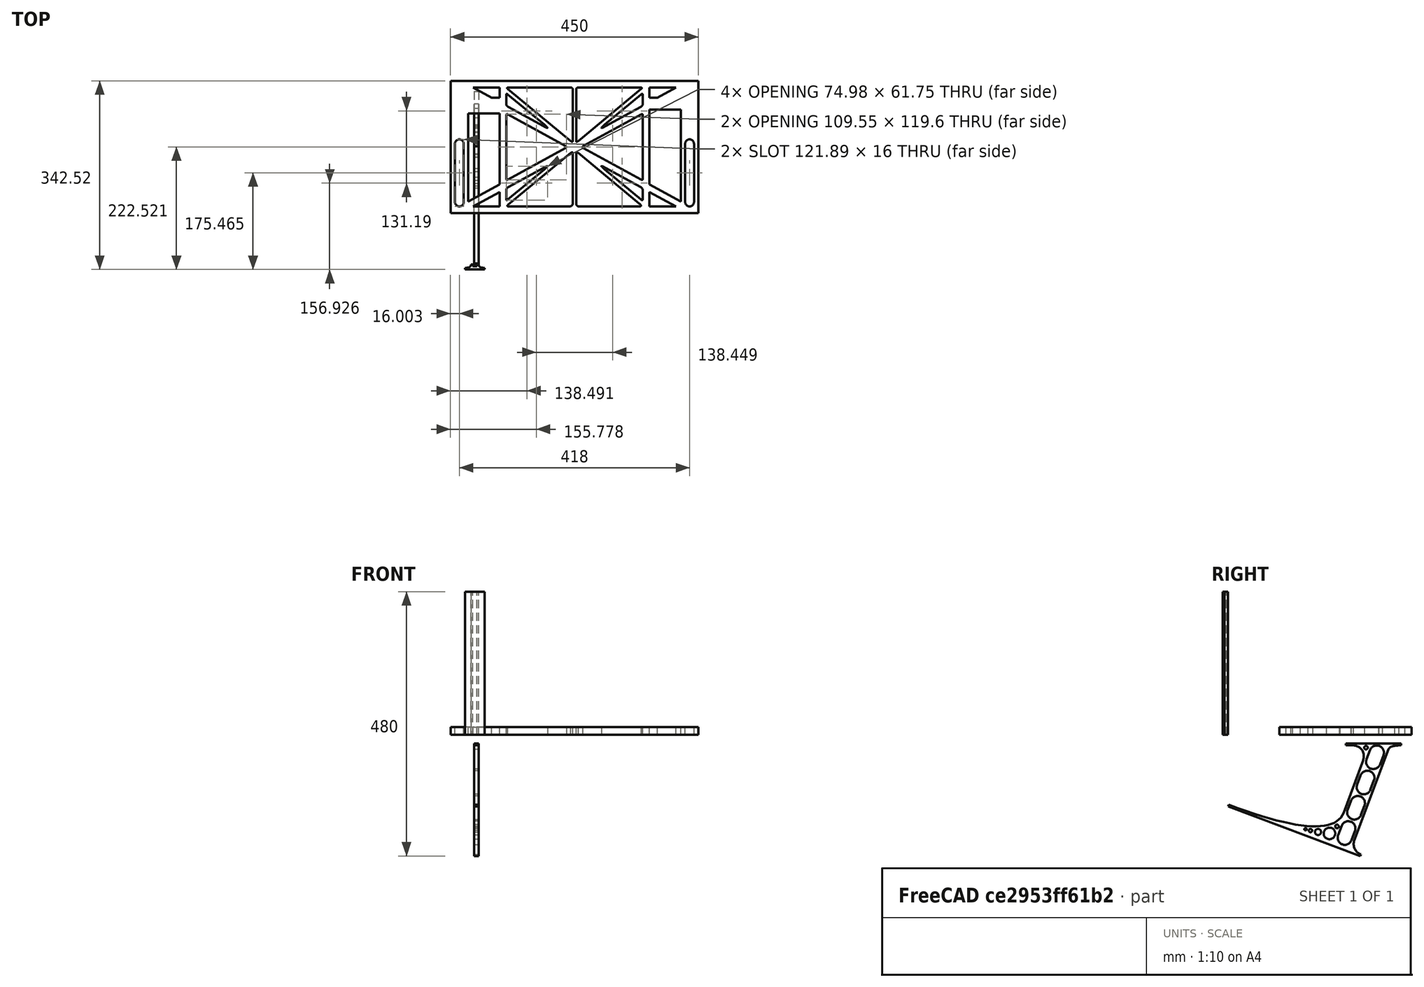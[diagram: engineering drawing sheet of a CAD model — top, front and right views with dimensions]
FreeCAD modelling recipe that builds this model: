
FCSTD DOCUMENT  (FreeCAD 0.19R0.19.2)
Label: laptopStand093
License: All rights reserved
LicenseURL: http://en.wikipedia.org/wiki/All_rights_reserved
objects: Sketcher::SketchObject×3, Part::Extrusion×3
note: 6 computed .brp shape members not serialized (recipe doc carries the construction recipe); baked Part::Feature solids carry a one-line shape summary decoded from their .brp

FEATURE [Sketcher::SketchObject] Sketch
  FullyConstrained = false
  sketch-geometry (252):
    g0: LineSegment StartX=-10.9272 StartY=-82.7794 StartZ=0 EndX=46.0728 EndY=-51.4823 EndZ=0
    g1: LineSegment StartX=366.073 StartY=-91.7794 StartZ=0 EndX=318.073 EndY=-65.424 EndZ=0
    g2: LineSegment StartX=-10.9272 StartY=77.3346 StartZ=0 EndX=-10.9272 EndY=-82.7794 EndZ=0
    g3: LineSegment StartX=375.073 StartY=-82.7794 StartZ=0 EndX=375.073 EndY=83.9235 EndZ=0
    g4: LineSegment StartX=-1.92719 StartY=-91.7794 StartZ=0 EndX=46.0728 EndY=-91.7794 EndZ=0
    g5: LineSegment StartX=318.073 StartY=124.221 StartZ=0 EndX=366.073 EndY=124.221 EndZ=0
    g6: LineSegment StartX=318.073 StartY=83.9235 StartZ=0 EndX=318.073 EndY=-51.4823 EndZ=0
    g7: LineSegment StartX=318.073 StartY=-51.4823 StartZ=0 EndX=375.073 EndY=-82.7794 EndZ=0
    g8: LineSegment StartX=318.073 StartY=-65.424 StartZ=0 EndX=318.073 EndY=-91.7794 EndZ=0
    g9: LineSegment StartX=318.073 StartY=-91.7794 StartZ=0 EndX=366.073 EndY=-91.7794 EndZ=0
    g10: LineSegment StartX=46.0728 StartY=-65.424 StartZ=0 EndX=-1.92719 EndY=-91.7794 EndZ=0
    g11: LineSegment StartX=46.0728 StartY=-65.424 StartZ=0 EndX=46.0728 EndY=-91.7794 EndZ=0
    g12: LineSegment StartX=46.0728 StartY=77.3346 StartZ=0 EndX=46.0728 EndY=-51.4823 EndZ=0
    g13: LineSegment StartX=-42.9272 StartY=136.221 StartZ=0 EndX=-42.9272 EndY=-103.779 EndZ=0
    g14: LineSegment StartX=407.073 StartY=136.221 StartZ=0 EndX=407.073 EndY=-103.779 EndZ=0
    g15: ArcOfCircle CenterX=-26.9272 CenterY=22.1087 CenterZ=0 NormalX=0 NormalY=0 NormalZ=1 AngleXU=0 Radius=8 StartAngle=1e-16 EndAngle=3.14159
    g16: ArcOfCircle CenterX=-26.9272 CenterY=-83.7794 CenterZ=0 NormalX=0 NormalY=0 NormalZ=1 AngleXU=0 Radius=8 StartAngle=3.14159 EndAngle=6.28319
    g17: LineSegment StartX=-34.9272 StartY=22.1087 StartZ=0 EndX=-34.9272 EndY=-83.7794 EndZ=0
    g18: LineSegment StartX=-18.9272 StartY=22.1087 StartZ=0 EndX=-18.9272 EndY=-83.7794 EndZ=0
    g19: ArcOfCircle CenterX=391.073 CenterY=22.1087 CenterZ=0 NormalX=0 NormalY=0 NormalZ=1 AngleXU=0 Radius=8 StartAngle=-4.4e-15 EndAngle=3.14159
    g20: LineSegment StartX=399.073 StartY=22.1087 StartZ=0 EndX=399.073 EndY=-83.7794 EndZ=0
    g21: LineSegment StartX=383.073 StartY=22.1087 StartZ=0 EndX=383.073 EndY=-83.7794 EndZ=0
    g22: ArcOfCircle CenterX=391.073 CenterY=-83.7794 CenterZ=0 NormalX=0 NormalY=0 NormalZ=1 AngleXU=0 Radius=8 StartAngle=3.14159 EndAngle=6.28319
    g23: Circle CenterX=175.022 CenterY=27.0628 CenterZ=0 NormalX=0 NormalY=0 NormalZ=1 AngleXU=0 Radius=1
    g24: Circle CenterX=179.022 CenterY=24.8665 CenterZ=0 NormalX=0 NormalY=0 NormalZ=1 AngleXU=0 Radius=1
    g25: Circle CenterX=179.022 CenterY=27.0628 CenterZ=0 NormalX=0 NormalY=0 NormalZ=1 AngleXU=0 Radius=1
    g26: BSplineCurve PolesCount=3 KnotsCount=2 Degree=2 IsPeriodic=0
    g27: GeomPoint X=175.022 Y=27.0628 Z=0
    g28: GeomPoint X=179.022 Y=27.0628 Z=0
    g29: Circle CenterX=189.124 CenterY=27.0628 CenterZ=0 NormalX=0 NormalY=0 NormalZ=1 AngleXU=0 Radius=1
    g30: Circle CenterX=185.124 CenterY=24.8665 CenterZ=0 NormalX=0 NormalY=0 NormalZ=1 AngleXU=0 Radius=1
    g31: Circle CenterX=185.124 CenterY=27.0628 CenterZ=0 NormalX=0 NormalY=0 NormalZ=1 AngleXU=0 Radius=1
    g32: BSplineCurve PolesCount=3 KnotsCount=2 Degree=2 IsPeriodic=0
    g33: GeomPoint X=189.124 Y=27.0628 Z=0
    g34: GeomPoint X=185.124 Y=27.0628 Z=0
    g35: Circle CenterX=175.022 CenterY=5.37834 CenterZ=0 NormalX=0 NormalY=0 NormalZ=1 AngleXU=0 Radius=1
    g36: Circle CenterX=179.022 CenterY=7.57463 CenterZ=0 NormalX=0 NormalY=0 NormalZ=1 AngleXU=0 Radius=1
    g37: Circle CenterX=179.022 CenterY=5.34704 CenterZ=0 NormalX=0 NormalY=0 NormalZ=1 AngleXU=0 Radius=1
    g38: BSplineCurve PolesCount=3 KnotsCount=2 Degree=2 IsPeriodic=0
    g39: GeomPoint X=175.022 Y=5.37834 Z=0
    g40: GeomPoint X=179.022 Y=5.34704 Z=0
    g41: Circle CenterX=189.124 CenterY=5.37834 CenterZ=0 NormalX=0 NormalY=0 NormalZ=1 AngleXU=0 Radius=1
    g42: Circle CenterX=185.124 CenterY=7.57463 CenterZ=0 NormalX=0 NormalY=0 NormalZ=1 AngleXU=0 Radius=1
    g43: Circle CenterX=185.124 CenterY=5.34704 CenterZ=0 NormalX=0 NormalY=0 NormalZ=1 AngleXU=0 Radius=1
    g44: BSplineCurve PolesCount=3 KnotsCount=2 Degree=2 IsPeriodic=0
    g45: GeomPoint X=189.124 Y=5.37834 Z=0
    g46: GeomPoint X=185.124 Y=5.34704 Z=0
    g47: Circle CenterX=165.871 CenterY=18.1458 CenterZ=0 NormalX=0 NormalY=0 NormalZ=1 AngleXU=0 Radius=1
    g48: Circle CenterX=169.377 CenterY=16.2206 CenterZ=0 NormalX=0 NormalY=0 NormalZ=1 AngleXU=0 Radius=1
    g49: Circle CenterX=165.871 CenterY=14.2954 CenterZ=0 NormalX=0 NormalY=0 NormalZ=1 AngleXU=0 Radius=1
    g50: BSplineCurve PolesCount=3 KnotsCount=2 Degree=2 IsPeriodic=0
    g51: GeomPoint X=165.871 Y=18.1458 Z=0
    g52: GeomPoint X=165.871 Y=14.2954 Z=0
    g53: Circle CenterX=198.275 CenterY=18.1458 CenterZ=0 NormalX=0 NormalY=0 NormalZ=1 AngleXU=0 Radius=1
    g54: Circle CenterX=194.768 CenterY=16.2206 CenterZ=0 NormalX=0 NormalY=0 NormalZ=1 AngleXU=0 Radius=1
    g55: Circle CenterX=198.275 CenterY=14.2954 CenterZ=0 NormalX=0 NormalY=0 NormalZ=1 AngleXU=0 Radius=1
    g56: BSplineCurve PolesCount=3 KnotsCount=2 Degree=2 IsPeriodic=0
    g57: GeomPoint X=198.275 Y=18.1458 Z=0
    g58: GeomPoint X=198.275 Y=14.2954 Z=0
    g59: LineSegment StartX=407.073 StartY=-103.779 StartZ=0 EndX=-42.9272 EndY=-103.779 EndZ=0
    g60: LineSegment StartX=407.073 StartY=136.221 StartZ=0 EndX=-42.9272 EndY=136.221 EndZ=0
    g61: LineSegment StartX=46.0728 StartY=77.3346 StartZ=0 EndX=-10.9272 EndY=77.3346 EndZ=0
    g62: LineSegment StartX=46.0728 StartY=105.865 StartZ=0 EndX=31.5028 EndY=105.865 EndZ=0
    g63: LineSegment StartX=46.0728 StartY=124.221 StartZ=0 EndX=46.0728 EndY=105.865 EndZ=0
    g64: LineSegment StartX=-1.92719 StartY=124.221 StartZ=0 EndX=31.5028 EndY=105.865 EndZ=0
    g65: LineSegment StartX=46.0728 StartY=124.221 StartZ=0 EndX=-1.92719 EndY=124.221 EndZ=0
    g66: LineSegment StartX=318.073 StartY=83.9235 StartZ=0 EndX=375.073 EndY=83.9235 EndZ=0
    g67: LineSegment StartX=318.073 StartY=105.865 StartZ=0 EndX=332.643 EndY=105.865 EndZ=0
    g68: LineSegment StartX=332.643 StartY=105.865 StartZ=0 EndX=366.073 EndY=124.221 EndZ=0
    g69: LineSegment StartX=318.073 StartY=124.221 StartZ=0 EndX=318.073 EndY=105.865 EndZ=0
    g70: Circle CenterX=125.607 CenterY=54.1951 CenterZ=0 NormalX=0 NormalY=0 NormalZ=1 AngleXU=0 Radius=1
    g71: Circle CenterX=139.632 CenterY=46.4944 CenterZ=0 NormalX=0 NormalY=0 NormalZ=1 AngleXU=0 Radius=1
    g72: Circle CenterX=127.326 CenterY=56.7187 CenterZ=0 NormalX=0 NormalY=0 NormalZ=1 AngleXU=0 Radius=1
    g73: BSplineCurve PolesCount=3 KnotsCount=2 Degree=2 IsPeriodic=0
    g74: GeomPoint X=125.607 Y=54.1951 Z=0
    g75: GeomPoint X=127.326 Y=56.7187 Z=0
    g76: Circle CenterX=236.821 CenterY=56.7187 CenterZ=0 NormalX=0 NormalY=0 NormalZ=1 AngleXU=0 Radius=1
    g77: Circle CenterX=224.513 CenterY=46.4944 CenterZ=0 NormalX=0 NormalY=0 NormalZ=1 AngleXU=0 Radius=1
    g78: Circle CenterX=238.538 CenterY=54.1951 CenterZ=0 NormalX=0 NormalY=0 NormalZ=1 AngleXU=0 Radius=1
    g79: BSplineCurve PolesCount=3 KnotsCount=2 Degree=2 IsPeriodic=0
    g80: GeomPoint X=236.821 Y=56.7187 Z=0
    g81: GeomPoint X=238.538 Y=54.1951 Z=0
    g82: Circle CenterX=238.538 CenterY=-21.7539 CenterZ=0 NormalX=0 NormalY=0 NormalZ=1 AngleXU=0 Radius=1
    g83: Circle CenterX=224.513 CenterY=-14.0532 CenterZ=0 NormalX=0 NormalY=0 NormalZ=1 AngleXU=0 Radius=1
    g84: Circle CenterX=236.821 CenterY=-24.2775 CenterZ=0 NormalX=0 NormalY=0 NormalZ=1 AngleXU=0 Radius=1
    g85: BSplineCurve PolesCount=3 KnotsCount=2 Degree=2 IsPeriodic=0
    g86: GeomPoint X=238.538 Y=-21.7539 Z=0
    g87: GeomPoint X=236.821 Y=-24.2775 Z=0
    g88: Circle CenterX=125.607 CenterY=-21.7539 CenterZ=0 NormalX=0 NormalY=0 NormalZ=1 AngleXU=0 Radius=1
    g89: Circle CenterX=139.632 CenterY=-14.0532 CenterZ=0 NormalX=0 NormalY=0 NormalZ=1 AngleXU=0 Radius=1
    g90: Circle CenterX=127.325 CenterY=-24.2775 CenterZ=0 NormalX=0 NormalY=0 NormalZ=1 AngleXU=0 Radius=1
    g91: BSplineCurve PolesCount=3 KnotsCount=2 Degree=2 IsPeriodic=0
    g92: GeomPoint X=125.607 Y=-21.7539 Z=0
    g93: GeomPoint X=127.325 Y=-24.2775 Z=0
    g94: Circle CenterX=302.996 CenterY=111.695 CenterZ=0 NormalX=0 NormalY=0 NormalZ=1 AngleXU=0 Radius=1
    g95: Circle CenterX=306.073 CenterY=114.251 CenterZ=0 NormalX=0 NormalY=0 NormalZ=1 AngleXU=0 Radius=1
    g96: Circle CenterX=306.073 CenterY=110.251 CenterZ=0 NormalX=0 NormalY=0 NormalZ=1 AngleXU=0 Radius=1
    g97: BSplineCurve PolesCount=3 KnotsCount=2 Degree=2 IsPeriodic=0
    g98: GeomPoint X=302.996 Y=111.695 Z=0
    g99: GeomPoint X=306.073 Y=110.251 Z=0
    g100: Circle CenterX=306.073 CenterY=95.2763 CenterZ=0 NormalX=0 NormalY=0 NormalZ=1 AngleXU=0 Radius=1
    g101: Circle CenterX=306.073 CenterY=91.2763 CenterZ=0 NormalX=0 NormalY=0 NormalZ=1 AngleXU=0 Radius=1
    g102: Circle CenterX=302.567 CenterY=89.3511 CenterZ=0 NormalX=0 NormalY=0 NormalZ=1 AngleXU=0 Radius=1
    g103: BSplineCurve PolesCount=3 KnotsCount=2 Degree=2 IsPeriodic=0
    g104: GeomPoint X=306.073 Y=95.2763 Z=0
    g105: GeomPoint X=302.567 Y=89.3511 Z=0
    g106: LineSegment StartX=306.073 StartY=110.251 StartZ=0 EndX=306.073 EndY=95.2763 EndZ=0
    g107: LineSegment StartX=302.996 StartY=111.695 StartZ=0 EndX=236.821 EndY=56.7187 EndZ=0
    g108: LineSegment StartX=238.538 StartY=54.1951 StartZ=0 EndX=302.567 EndY=89.3511 EndZ=0
    g109: Circle CenterX=61.1496 CenterY=111.695 CenterZ=0 NormalX=0 NormalY=0 NormalZ=1 AngleXU=0 Radius=1
    g110: Circle CenterX=58.0728 CenterY=114.251 CenterZ=0 NormalX=0 NormalY=0 NormalZ=1 AngleXU=0 Radius=1
    g111: Circle CenterX=58.0728 CenterY=110.251 CenterZ=0 NormalX=0 NormalY=0 NormalZ=1 AngleXU=0 Radius=1
    g112: BSplineCurve PolesCount=3 KnotsCount=2 Degree=2 IsPeriodic=0
    g113: GeomPoint X=61.1496 Y=111.695 Z=0
    g114: GeomPoint X=58.0728 Y=110.251 Z=0
    g115: Circle CenterX=61.5791 CenterY=89.3511 CenterZ=0 NormalX=0 NormalY=0 NormalZ=1 AngleXU=0 Radius=1
    g116: Circle CenterX=58.0728 CenterY=91.2763 CenterZ=0 NormalX=0 NormalY=0 NormalZ=1 AngleXU=0 Radius=1
    g117: Circle CenterX=58.0728 CenterY=95.2763 CenterZ=0 NormalX=0 NormalY=0 NormalZ=1 AngleXU=0 Radius=1
    g118: BSplineCurve PolesCount=3 KnotsCount=2 Degree=2 IsPeriodic=0
    g119: GeomPoint X=61.5791 Y=89.3511 Z=0
    g120: GeomPoint X=58.0728 Y=95.2763 Z=0
    g121: LineSegment StartX=58.0728 StartY=110.251 StartZ=0 EndX=58.0728 EndY=95.2763 EndZ=0
    g122: LineSegment StartX=61.1496 StartY=111.695 StartZ=0 EndX=127.326 EndY=56.7187 EndZ=0
    g123: LineSegment StartX=125.607 StartY=54.1951 StartZ=0 EndX=61.5791 EndY=89.3511 EndZ=0
    g124: Circle CenterX=61.5791 CenterY=-56.9099 CenterZ=0 NormalX=0 NormalY=0 NormalZ=1 AngleXU=0 Radius=1
    g125: Circle CenterX=58.0728 CenterY=-58.8351 CenterZ=0 NormalX=0 NormalY=0 NormalZ=1 AngleXU=0 Radius=1
    g126: Circle CenterX=58.0728 CenterY=-62.8351 CenterZ=0 NormalX=0 NormalY=0 NormalZ=1 AngleXU=0 Radius=1
    g127: BSplineCurve PolesCount=3 KnotsCount=2 Degree=2 IsPeriodic=0
    g128: GeomPoint X=61.5791 Y=-56.9099 Z=0
    g129: GeomPoint X=58.0728 Y=-62.8351 Z=0
    g130: Circle CenterX=58.0728 CenterY=-77.8102 CenterZ=0 NormalX=0 NormalY=0 NormalZ=1 AngleXU=0 Radius=1
    g131: Circle CenterX=58.0728 CenterY=-81.8102 CenterZ=0 NormalX=0 NormalY=0 NormalZ=1 AngleXU=0 Radius=1
    g132: Circle CenterX=61.1496 CenterY=-79.2541 CenterZ=0 NormalX=0 NormalY=0 NormalZ=1 AngleXU=0 Radius=1
    g133: BSplineCurve PolesCount=3 KnotsCount=2 Degree=2 IsPeriodic=0
    g134: GeomPoint X=58.0728 Y=-77.8102 Z=0
    g135: GeomPoint X=61.1496 Y=-79.2541 Z=0
    g136: LineSegment StartX=58.0728 StartY=-62.8351 StartZ=0 EndX=58.0728 EndY=-77.8102 EndZ=0
    g137: LineSegment StartX=61.1496 StartY=-79.2541 StartZ=0 EndX=127.325 EndY=-24.2775 EndZ=0
    g138: LineSegment StartX=125.607 StartY=-21.7539 StartZ=0 EndX=61.5791 EndY=-56.9099 EndZ=0
    g139: Circle CenterX=302.567 CenterY=-56.9099 CenterZ=0 NormalX=0 NormalY=0 NormalZ=1 AngleXU=0 Radius=1
    g140: Circle CenterX=306.073 CenterY=-58.8351 CenterZ=0 NormalX=0 NormalY=0 NormalZ=1 AngleXU=0 Radius=1
    g141: Circle CenterX=306.073 CenterY=-62.8351 CenterZ=0 NormalX=0 NormalY=0 NormalZ=1 AngleXU=0 Radius=1
    g142: BSplineCurve PolesCount=3 KnotsCount=2 Degree=2 IsPeriodic=0
    g143: GeomPoint X=302.567 Y=-56.9099 Z=0
    g144: GeomPoint X=306.073 Y=-62.8351 Z=0
    g145: Circle CenterX=302.996 CenterY=-79.2541 CenterZ=0 NormalX=0 NormalY=0 NormalZ=1 AngleXU=0 Radius=1
    g146: Circle CenterX=306.073 CenterY=-81.8102 CenterZ=0 NormalX=0 NormalY=0 NormalZ=1 AngleXU=0 Radius=1
    g147: Circle CenterX=306.073 CenterY=-77.8102 CenterZ=0 NormalX=0 NormalY=0 NormalZ=1 AngleXU=0 Radius=1
    g148: BSplineCurve PolesCount=3 KnotsCount=2 Degree=2 IsPeriodic=0
    g149: GeomPoint X=302.996 Y=-79.2541 Z=0
    g150: GeomPoint X=306.073 Y=-77.8102 Z=0
    g151: LineSegment StartX=306.073 StartY=-62.8351 StartZ=0 EndX=306.073 EndY=-77.8102 EndZ=0
    g152: LineSegment StartX=302.996 StartY=-79.2541 StartZ=0 EndX=236.821 EndY=-24.2775 EndZ=0
    g153: LineSegment StartX=238.538 StartY=-21.7539 StartZ=0 EndX=302.567 EndY=-56.9099 EndZ=0
    g154: Circle CenterX=61.6457 CenterY=-88.8112 CenterZ=0 NormalX=0 NormalY=0 NormalZ=1 AngleXU=0 Radius=1
    g155: Circle CenterX=58.0728 CenterY=-91.7794 CenterZ=0 NormalX=0 NormalY=0 NormalZ=1 AngleXU=0 Radius=1
    g156: Circle CenterX=63.9135 CenterY=-91.7794 CenterZ=0 NormalX=0 NormalY=0 NormalZ=1 AngleXU=0 Radius=1
    g157: BSplineCurve PolesCount=3 KnotsCount=2 Degree=2 IsPeriodic=0
    g158: GeomPoint X=61.6457 Y=-88.8112 Z=0
    g159: GeomPoint X=63.9135 Y=-91.7794 Z=0
    g160: Circle CenterX=179.022 CenterY=-85.8163 CenterZ=0 NormalX=0 NormalY=0 NormalZ=1 AngleXU=0 Radius=1
    g161: Circle CenterX=179.022 CenterY=-91.7794 CenterZ=0 NormalX=0 NormalY=0 NormalZ=1 AngleXU=0 Radius=1
    g162: Circle CenterX=171.895 CenterY=-91.7794 CenterZ=0 NormalX=0 NormalY=0 NormalZ=1 AngleXU=0 Radius=1
    g163: BSplineCurve PolesCount=3 KnotsCount=2 Degree=2 IsPeriodic=0
    g164: GeomPoint X=179.022 Y=-85.8163 Z=0
    g165: GeomPoint X=171.895 Y=-91.7794 Z=0
    g166: Circle CenterX=185.124 CenterY=-86.2028 CenterZ=0 NormalX=0 NormalY=0 NormalZ=1 AngleXU=0 Radius=1
    g167: Circle CenterX=185.124 CenterY=-91.7794 CenterZ=0 NormalX=0 NormalY=0 NormalZ=1 AngleXU=0 Radius=1
    g168: Circle CenterX=191.747 CenterY=-91.7794 CenterZ=0 NormalX=0 NormalY=0 NormalZ=1 AngleXU=0 Radius=1
    g169: BSplineCurve PolesCount=3 KnotsCount=2 Degree=2 IsPeriodic=0
    g170: GeomPoint X=185.124 Y=-86.2028 Z=0
    g171: GeomPoint X=191.747 Y=-91.7794 Z=0
    g172: Circle CenterX=299.888 CenterY=-86.6413 CenterZ=0 NormalX=0 NormalY=0 NormalZ=1 AngleXU=0 Radius=1
    g173: Circle CenterX=306.073 CenterY=-91.7794 CenterZ=0 NormalX=0 NormalY=0 NormalZ=1 AngleXU=0 Radius=1
    g174: Circle CenterX=298.776 CenterY=-91.7794 CenterZ=0 NormalX=0 NormalY=0 NormalZ=1 AngleXU=0 Radius=1
    g175: BSplineCurve PolesCount=3 KnotsCount=2 Degree=2 IsPeriodic=0
    g176: GeomPoint X=299.888 Y=-86.6413 Z=0
    g177: GeomPoint X=298.776 Y=-91.7794 Z=0
    g178: LineSegment StartX=189.124 StartY=5.37834 StartZ=0 EndX=299.888 EndY=-86.6413 EndZ=0
    g179: LineSegment StartX=298.776 StartY=-91.7794 StartZ=0 EndX=191.747 EndY=-91.7794 EndZ=0
    g180: LineSegment StartX=185.124 StartY=-86.2028 StartZ=0 EndX=185.124 EndY=5.34704 EndZ=0
    g181: LineSegment StartX=179.022 StartY=5.34704 StartZ=0 EndX=179.022 EndY=-85.8163 EndZ=0
    g182: LineSegment StartX=171.895 StartY=-91.7794 StartZ=0 EndX=63.9135 EndY=-91.7794 EndZ=0
    g183: LineSegment StartX=61.6457 StartY=-88.8112 StartZ=0 EndX=175.022 EndY=5.37834 EndZ=0
    g184: Circle CenterX=302.073 CenterY=124.221 CenterZ=0 NormalX=0 NormalY=0 NormalZ=1 AngleXU=0 Radius=1
    g185: Circle CenterX=306.073 CenterY=124.221 CenterZ=0 NormalX=0 NormalY=0 NormalZ=1 AngleXU=0 Radius=1
    g186: Circle CenterX=302.996 CenterY=121.665 CenterZ=0 NormalX=0 NormalY=0 NormalZ=1 AngleXU=0 Radius=1
    g187: BSplineCurve PolesCount=3 KnotsCount=2 Degree=2 IsPeriodic=0
    g188: GeomPoint X=302.073 Y=124.221 Z=0
    g189: GeomPoint X=302.996 Y=121.665 Z=0
    g190: Circle CenterX=189.124 CenterY=124.221 CenterZ=0 NormalX=0 NormalY=0 NormalZ=1 AngleXU=0 Radius=1
    g191: Circle CenterX=185.124 CenterY=124.221 CenterZ=0 NormalX=0 NormalY=0 NormalZ=1 AngleXU=0 Radius=1
    g192: Circle CenterX=185.124 CenterY=120.221 CenterZ=0 NormalX=0 NormalY=0 NormalZ=1 AngleXU=0 Radius=1
    g193: BSplineCurve PolesCount=3 KnotsCount=2 Degree=2 IsPeriodic=0
    g194: GeomPoint X=189.124 Y=124.221 Z=0
    g195: GeomPoint X=185.124 Y=120.221 Z=0
    g196: Circle CenterX=175.022 CenterY=124.221 CenterZ=0 NormalX=0 NormalY=0 NormalZ=1 AngleXU=0 Radius=1
    g197: Circle CenterX=179.022 CenterY=124.221 CenterZ=0 NormalX=0 NormalY=0 NormalZ=1 AngleXU=0 Radius=1
    g198: Circle CenterX=179.022 CenterY=120.221 CenterZ=0 NormalX=0 NormalY=0 NormalZ=1 AngleXU=0 Radius=1
    g199: BSplineCurve PolesCount=3 KnotsCount=2 Degree=2 IsPeriodic=0
    g200: GeomPoint X=175.022 Y=124.221 Z=0
    g201: GeomPoint X=179.022 Y=120.221 Z=0
    g202: Circle CenterX=62.0728 CenterY=124.221 CenterZ=0 NormalX=0 NormalY=0 NormalZ=1 AngleXU=0 Radius=1
    g203: Circle CenterX=58.0728 CenterY=124.221 CenterZ=0 NormalX=0 NormalY=0 NormalZ=1 AngleXU=0 Radius=1
    g204: Circle CenterX=61.1496 CenterY=121.665 CenterZ=0 NormalX=0 NormalY=0 NormalZ=1 AngleXU=0 Radius=1
    g205: BSplineCurve PolesCount=3 KnotsCount=2 Degree=2 IsPeriodic=0
    g206: GeomPoint X=62.0728 Y=124.221 Z=0
    g207: GeomPoint X=61.1496 Y=121.665 Z=0
    g208: LineSegment StartX=62.0728 StartY=124.221 StartZ=0 EndX=175.022 EndY=124.221 EndZ=0
    g209: LineSegment StartX=179.022 StartY=120.221 StartZ=0 EndX=179.022 EndY=27.0628 EndZ=0
    g210: LineSegment StartX=185.124 StartY=27.0628 StartZ=0 EndX=185.124 EndY=120.221 EndZ=0
    g211: LineSegment StartX=189.124 StartY=124.221 StartZ=0 EndX=302.073 EndY=124.221 EndZ=0
    g212: LineSegment StartX=302.996 StartY=121.665 StartZ=0 EndX=189.124 EndY=27.0628 EndZ=0
    g213: LineSegment StartX=175.022 StartY=27.0628 StartZ=0 EndX=61.1496 EndY=121.665 EndZ=0
    g214: Circle CenterX=61.5791 CenterY=75.4095 CenterZ=0 NormalX=0 NormalY=0 NormalZ=1 AngleXU=0 Radius=1
    g215: Circle CenterX=58.0728 CenterY=77.3346 CenterZ=0 NormalX=0 NormalY=0 NormalZ=1 AngleXU=0 Radius=1
    g216: Circle CenterX=58.0728 CenterY=73.3346 CenterZ=0 NormalX=0 NormalY=0 NormalZ=1 AngleXU=0 Radius=1
    g217: BSplineCurve PolesCount=3 KnotsCount=2 Degree=2 IsPeriodic=0
    g218: GeomPoint X=61.5791 Y=75.4095 Z=0
    g219: GeomPoint X=58.0728 Y=73.3346 Z=0
    g220: Circle CenterX=58.0728 CenterY=-40.8935 CenterZ=0 NormalX=0 NormalY=0 NormalZ=1 AngleXU=0 Radius=1
    g221: Circle CenterX=58.0728 CenterY=-44.8935 CenterZ=0 NormalX=0 NormalY=0 NormalZ=1 AngleXU=0 Radius=1
    g222: Circle CenterX=61.5791 CenterY=-42.9683 CenterZ=0 NormalX=0 NormalY=0 NormalZ=1 AngleXU=0 Radius=1
    g223: BSplineCurve PolesCount=3 KnotsCount=2 Degree=2 IsPeriodic=0
    g224: GeomPoint X=58.0728 Y=-40.8935 Z=0
    g225: GeomPoint X=61.5791 Y=-42.9683 Z=0
    g226: LineSegment StartX=61.5791 StartY=-42.9683 StartZ=0 EndX=165.871 EndY=14.2954 EndZ=0
    g227: LineSegment StartX=165.871 StartY=18.1458 StartZ=0 EndX=61.5791 EndY=75.4095 EndZ=0
    g228: LineSegment StartX=58.0728 StartY=73.3346 StartZ=0 EndX=58.0728 EndY=-40.8935 EndZ=0
    g229: Circle CenterX=302.567 CenterY=-42.9683 CenterZ=0 NormalX=0 NormalY=0 NormalZ=1 AngleXU=0 Radius=1
    g230: Circle CenterX=306.073 CenterY=-44.8935 CenterZ=0 NormalX=0 NormalY=0 NormalZ=1 AngleXU=0 Radius=1
    g231: Circle CenterX=306.073 CenterY=-40.8935 CenterZ=0 NormalX=0 NormalY=0 NormalZ=1 AngleXU=0 Radius=1
    g232: BSplineCurve PolesCount=3 KnotsCount=2 Degree=2 IsPeriodic=0
    g233: GeomPoint X=302.567 Y=-42.9683 Z=0
    g234: GeomPoint X=306.073 Y=-40.8935 Z=0
    g235: Circle CenterX=306.073 CenterY=73.3346 CenterZ=0 NormalX=0 NormalY=0 NormalZ=1 AngleXU=0 Radius=1
    g236: Circle CenterX=306.073 CenterY=77.3346 CenterZ=0 NormalX=0 NormalY=0 NormalZ=1 AngleXU=0 Radius=1
    g237: Circle CenterX=302.567 CenterY=75.4095 CenterZ=0 NormalX=0 NormalY=0 NormalZ=1 AngleXU=0 Radius=1
    g238: BSplineCurve PolesCount=3 KnotsCount=2 Degree=2 IsPeriodic=0
    g239: GeomPoint X=306.073 Y=73.3346 Z=0
    g240: GeomPoint X=302.567 Y=75.4095 Z=0
    g241: LineSegment StartX=302.567 StartY=-42.9683 StartZ=0 EndX=198.275 EndY=14.2954 EndZ=0
    g242: LineSegment StartX=198.275 StartY=18.1458 StartZ=0 EndX=302.567 EndY=75.4095 EndZ=0
    g243: LineSegment StartX=306.073 StartY=73.3346 StartZ=0 EndX=306.073 EndY=-40.8935 EndZ=0
    g244: LineSegment StartX=319.904 StartY=125.546 StartZ=0 EndX=323.904 EndY=125.546 EndZ=0
    g245: LineSegment StartX=364.483 StartY=125.086 StartZ=0 EndX=360.483 EndY=125.086 EndZ=0
    g246: LineSegment StartX=327.931 StartY=104.661 StartZ=0 EndX=331.931 EndY=104.661 EndZ=0
    g247: LineSegment StartX=335.6 StartY=105.351 StartZ=0 EndX=339.311 EndY=107.624 EndZ=0
    g248: LineSegment StartX=366.554 StartY=122.928 StartZ=0 EndX=363.62 EndY=120.771 EndZ=0
    g249: LineSegment StartX=317.217 StartY=106.631 StartZ=0 EndX=317.217 EndY=110.631 EndZ=0
    g250: LineSegment StartX=318.286 StartY=104.747 StartZ=0 EndX=322.286 EndY=104.747 EndZ=0
    g251: LineSegment StartX=317.131 StartY=123.912 StartZ=0 EndX=317.131 EndY=119.912 EndZ=0
  constraints (427):
    c: Horizontal(g4)
    c: Horizontal(g5)
    c: Coincident(g6,g7)
    c: Coincident(g8,g1)
    c: Tangent(g6,g8)
    c: Coincident(g11,g10)
    c: Coincident(g0,g12)
    c: Block(g7)
    c: Block(g3)
    c: Block(g1)
    c: Block(g8)
    c: Block(g11)
    c: Block(g10)
    c: Block(g0)
    c: Block(g2)
    c: Block(g5)
    c: Block(g9)
    c: Block(g4)
    c: Vertical(g13)
    c: Vertical(g14)
    c: Block(g14)
    c: Block(g13)
    c: Tangent(g15,g18) = 1.5708
    c: Tangent(g15,g17) = -1.5708
    c: Tangent(g17,g16) = -1.5708
    c: Tangent(g18,g16) = 1.5708
    c: Vertical(g17)
    c: Equal(g15,g16)
    c: Block(g18)
    c: Block(g17)
    c: Tangent(g19,g20) = 1.5708
    c: Tangent(g20,g22) = 1.5708
    c: Equal(g19,g22)
    c: Coincident(g21,g19)
    c: Coincident(g21,g22)
    c: Block(g20)
    c: Block(g21)
    c: Weight(g23) = 1
    c: Equal(g23,g24)
    c: Equal(g23,g25)
    c: InternalAlignment(g23,g26)
    c: InternalAlignment(g24,g26)
    c: InternalAlignment(g25,g26)
    c: InternalAlignment(g27,g26)
    c: InternalAlignment(g28,g26)
    c: Weight(g29) = 1
    c: Equal(g29,g30)
    c: Equal(g29,g31)
    c: InternalAlignment(g29,g32)
    c: InternalAlignment(g30,g32)
    c: InternalAlignment(g31,g32)
    c: InternalAlignment(g33,g32)
    c: InternalAlignment(g34,g32)
    c: Block(g32)
    c: Block(g26)
    c: Weight(g35) = 1
    c: Equal(g35,g36)
    c: Equal(g35,g37)
    c: InternalAlignment(g35,g38)
    c: InternalAlignment(g36,g38)
    c: InternalAlignment(g37,g38)
    c: InternalAlignment(g39,g38)
    c: InternalAlignment(g40,g38)
    c: Weight(g41) = 1
    c: Equal(g41,g42)
    c: Equal(g41,g43)
    c: InternalAlignment(g41,g44)
    c: InternalAlignment(g42,g44)
    c: InternalAlignment(g43,g44)
    c: InternalAlignment(g45,g44)
    c: InternalAlignment(g46,g44)
    c: Block(g44)
    c: Block(g38)
    c: Weight(g47) = 1
    c: Equal(g47,g48)
    c: Equal(g47,g49)
    c: InternalAlignment(g47,g50)
    c: InternalAlignment(g48,g50)
    c: InternalAlignment(g49,g50)
    c: InternalAlignment(g51,g50)
    c: InternalAlignment(g52,g50)
    c: Weight(g53) = 1
    c: Equal(g53,g54)
    c: Equal(g53,g55)
    c: InternalAlignment(g53,g56)
    c: InternalAlignment(g54,g56)
    c: InternalAlignment(g55,g56)
    c: InternalAlignment(g57,g56)
    c: InternalAlignment(g58,g56)
    c: Block(g50)
    c: Block(g56)
    c: Coincident(g59,g14)
    c: Coincident(g59,g13)
    c: Horizontal(g59)
    c: Distance(g59) = 450
    c: Coincident(g60,g14)
    c: Coincident(g60,g13)
    c: Horizontal(g60)
    c: Horizontal(g61)
    c: Coincident(g12,g61)
    c: Horizontal(g62)
    c: Vertical(g63)
    c: Block(g63)
    c: Block(g62)
    c: Block(g61)
    c: Distance(g63) = 18.3554
    c: Coincident(g65,g63)
    c: Coincident(g65,g64)
    c: Horizontal(g65)
    c: Block(g65)
    c: Block(g64)
    c: Coincident(g62,g64)
    c: Coincident(g2,g61)
    c: Coincident(g66,g6)
    c: Horizontal(g66)
    c: Horizontal(g67)
    c: Block(g66)
    c: Coincident(g68,g5)
    c: Coincident(g69,g5)
    c: Coincident(g69,g67)
    c: Vertical(g69)
    c: Block(g69)
    c: Coincident(g67,g68)
    c: Block(g68)
    c: Coincident(g3,g66)
    c: Weight(g70) = 1
    c: Equal(g70,g71)
    c: Equal(g70,g72)
    c: InternalAlignment(g70,g73)
    c: InternalAlignment(g71,g73)
    c: InternalAlignment(g72,g73)
    c: InternalAlignment(g74,g73)
    c: InternalAlignment(g75,g73)
    c: Block(g73)
    c: Weight(g76) = 1
    c: Equal(g76,g77)
    c: Equal(g76,g78)
    c: InternalAlignment(g76,g79)
    c: InternalAlignment(g77,g79)
    c: InternalAlignment(g78,g79)
    c: InternalAlignment(g80,g79)
    c: InternalAlignment(g81,g79)
    c: Block(g79)
    c: Weight(g82) = 1
    c: Equal(g82,g83)
    c: Equal(g82,g84)
    c: InternalAlignment(g82,g85)
    c: InternalAlignment(g83,g85)
    c: InternalAlignment(g84,g85)
    c: InternalAlignment(g86,g85)
    c: InternalAlignment(g87,g85)
    c: Block(g85)
    c: Weight(g88) = 1
    c: Equal(g88,g89)
    c: Equal(g88,g90)
    c: InternalAlignment(g88,g91)
    c: InternalAlignment(g89,g91)
    c: InternalAlignment(g90,g91)
    c: InternalAlignment(g92,g91)
    c: InternalAlignment(g93,g91)
    c: Block(g91)
    c: Weight(g94) = 1
    c: Equal(g94,g95)
    c: Equal(g94,g96)
    c: InternalAlignment(g94,g97)
    c: InternalAlignment(g95,g97)
    c: InternalAlignment(g96,g97)
    c: InternalAlignment(g98,g97)
    c: InternalAlignment(g99,g97)
    c: Weight(g100) = 1
    c: Equal(g100,g101)
    c: Equal(g100,g102)
    c: InternalAlignment(g100,g103)
    c: InternalAlignment(g101,g103)
    c: InternalAlignment(g102,g103)
    c: InternalAlignment(g104,g103)
    c: InternalAlignment(g105,g103)
    c: Block(g97)
    c: Block(g103)
    c: Coincident(g106,g97)
    c: Coincident(g106,g103)
    c: Vertical(g106)
    c: Coincident(g107,g97)
    c: Coincident(g107,g79)
    c: Coincident(g108,g79)
    c: Coincident(g108,g103)
    c: Weight(g109) = 1
    c: Equal(g109,g110)
    c: Equal(g109,g111)
    c: InternalAlignment(g109,g112)
    c: InternalAlignment(g110,g112)
    c: InternalAlignment(g111,g112)
    c: InternalAlignment(g113,g112)
    c: InternalAlignment(g114,g112)
    c: Weight(g115) = 1
    c: Equal(g115,g116)
    c: Equal(g115,g117)
    c: InternalAlignment(g115,g118)
    c: InternalAlignment(g116,g118)
    c: InternalAlignment(g117,g118)
    c: InternalAlignment(g119,g118)
    c: InternalAlignment(g120,g118)
    c: Block(g112)
    c: Block(g118)
    c: Coincident(g121,g112)
    c: Coincident(g121,g118)
    c: Vertical(g121)
    c: Coincident(g122,g112)
    c: Coincident(g122,g73)
    c: Coincident(g123,g73)
    c: Coincident(g123,g118)
    c: Weight(g124) = 1
    c: Equal(g124,g125)
    c: Equal(g124,g126)
    c: InternalAlignment(g124,g127)
    c: InternalAlignment(g125,g127)
    c: InternalAlignment(g126,g127)
    c: InternalAlignment(g128,g127)
    c: InternalAlignment(g129,g127)
    c: Weight(g130) = 1
    c: Equal(g130,g131)
    c: Equal(g130,g132)
    c: InternalAlignment(g130,g133)
    c: InternalAlignment(g131,g133)
    c: InternalAlignment(g132,g133)
    c: InternalAlignment(g134,g133)
    c: InternalAlignment(g135,g133)
    c: Block(g127)
    c: Block(g133)
    c: Coincident(g136,g127)
    c: Coincident(g136,g133)
    c: Vertical(g136)
    c: Coincident(g137,g133)
    c: Coincident(g137,g91)
    c: Coincident(g138,g91)
    c: Coincident(g138,g127)
    c: Weight(g139) = 1
    c: Equal(g139,g140)
    c: Equal(g139,g141)
    c: InternalAlignment(g139,g142)
    c: InternalAlignment(g140,g142)
    c: InternalAlignment(g141,g142)
    c: InternalAlignment(g143,g142)
    c: InternalAlignment(g144,g142)
    c: Weight(g145) = 1
    c: Equal(g145,g146)
    c: Equal(g145,g147)
    c: InternalAlignment(g145,g148)
    c: InternalAlignment(g146,g148)
    c: InternalAlignment(g147,g148)
    c: InternalAlignment(g149,g148)
    c: InternalAlignment(g150,g148)
    c: Block(g142)
    c: Block(g148)
    c: Coincident(g151,g142)
    c: Coincident(g151,g148)
    c: Vertical(g151)
    c: Coincident(g152,g148)
    c: Coincident(g152,g85)
    c: Coincident(g153,g85)
    c: Coincident(g153,g142)
    c: Weight(g154) = 1
    c: Equal(g154,g155)
    c: Equal(g154,g156)
    c: InternalAlignment(g154,g157)
    c: InternalAlignment(g155,g157)
    c: InternalAlignment(g156,g157)
    c: InternalAlignment(g158,g157)
    c: InternalAlignment(g159,g157)
    c: Weight(g160) = 1
    c: Equal(g160,g161)
    c: Equal(g160,g162)
    c: InternalAlignment(g160,g163)
    c: InternalAlignment(g161,g163)
    c: InternalAlignment(g162,g163)
    c: InternalAlignment(g164,g163)
    c: InternalAlignment(g165,g163)
    c: Weight(g166) = 1
    c: Equal(g166,g167)
    c: Equal(g166,g168)
    c: InternalAlignment(g166,g169)
    c: InternalAlignment(g167,g169)
    c: InternalAlignment(g168,g169)
    c: InternalAlignment(g170,g169)
    c: InternalAlignment(g171,g169)
    c: Weight(g172) = 1
    c: Equal(g172,g173)
    c: Equal(g172,g174)
    c: InternalAlignment(g172,g175)
    c: InternalAlignment(g173,g175)
    c: InternalAlignment(g174,g175)
    c: InternalAlignment(g176,g175)
    c: InternalAlignment(g177,g175)
    c: Block(g175)
    c: Block(g169)
    c: Block(g163)
    c: Block(g157)
    c: Coincident(g178,g44)
    c: Coincident(g178,g175)
    c: Coincident(g179,g175)
    c: Coincident(g179,g169)
    c: Horizontal(g179)
    c: Coincident(g180,g169)
    c: Coincident(g180,g44)
    c: Vertical(g180)
    c: Coincident(g181,g38)
    c: Coincident(g181,g163)
    c: Vertical(g181)
    c: Coincident(g182,g163)
    c: Coincident(g182,g157)
    c: Horizontal(g182)
    c: Coincident(g183,g157)
    c: Coincident(g183,g38)
    c: Weight(g184) = 1
    c: Equal(g184,g185)
    c: Equal(g184,g186)
    c: InternalAlignment(g184,g187)
    c: InternalAlignment(g185,g187)
    c: InternalAlignment(g186,g187)
    c: InternalAlignment(g188,g187)
    c: InternalAlignment(g189,g187)
    c: Weight(g190) = 1
    c: Equal(g190,g191)
    c: Equal(g190,g192)
    c: InternalAlignment(g190,g193)
    c: InternalAlignment(g191,g193)
    c: InternalAlignment(g192,g193)
    c: InternalAlignment(g194,g193)
    c: InternalAlignment(g195,g193)
    c: Weight(g196) = 1
    c: Equal(g196,g197)
    c: Equal(g196,g198)
    c: InternalAlignment(g196,g199)
    c: InternalAlignment(g197,g199)
    c: InternalAlignment(g198,g199)
    c: InternalAlignment(g200,g199)
    c: InternalAlignment(g201,g199)
    c: Weight(g202) = 1
    c: Equal(g202,g203)
    c: Equal(g202,g204)
    c: InternalAlignment(g202,g205)
    c: InternalAlignment(g203,g205)
    c: InternalAlignment(g204,g205)
    c: InternalAlignment(g206,g205)
    c: InternalAlignment(g207,g205)
    c: Block(g205)
    c: Block(g199)
    c: Block(g193)
    c: Block(g187)
    c: Coincident(g208,g205)
    c: Coincident(g208,g199)
    c: Horizontal(g208)
    c: Coincident(g209,g199)
    c: Coincident(g209,g26)
    c: Vertical(g209)
    c: Coincident(g210,g32)
    c: Coincident(g210,g193)
    c: Vertical(g210)
    c: Coincident(g211,g193)
    c: Coincident(g211,g187)
    c: Horizontal(g211)
    c: Coincident(g212,g187)
    c: Coincident(g212,g32)
    c: Coincident(g213,g26)
    c: Coincident(g213,g205)
    c: Weight(g214) = 1
    c: Equal(g214,g215)
    c: Equal(g214,g216)
    c: InternalAlignment(g214,g217)
    c: InternalAlignment(g215,g217)
    c: InternalAlignment(g216,g217)
    c: InternalAlignment(g218,g217)
    c: InternalAlignment(g219,g217)
    c: Weight(g220) = 1
    c: Equal(g220,g221)
    c: Equal(g220,g222)
    c: InternalAlignment(g220,g223)
    c: InternalAlignment(g221,g223)
    c: InternalAlignment(g222,g223)
    c: InternalAlignment(g224,g223)
    c: InternalAlignment(g225,g223)
    c: Block(g223)
    c: Block(g217)
    c: Coincident(g226,g223)
    c: Coincident(g226,g50)
    c: Coincident(g227,g50)
    c: Coincident(g227,g217)
    c: Coincident(g228,g217)
    c: Coincident(g228,g223)
    c: Vertical(g228)
    c: Weight(g229) = 1
    c: Equal(g229,g230)
    c: Equal(g229,g231)
    c: InternalAlignment(g229,g232)
    c: InternalAlignment(g230,g232)
    c: InternalAlignment(g231,g232)
    c: InternalAlignment(g233,g232)
    c: InternalAlignment(g234,g232)
    c: Weight(g235) = 1
    c: Equal(g235,g236)
    c: Equal(g235,g237)
    c: InternalAlignment(g235,g238)
    c: InternalAlignment(g236,g238)
    c: InternalAlignment(g237,g238)
    c: InternalAlignment(g239,g238)
    c: InternalAlignment(g240,g238)
    c: Block(g238)
    c: Block(g232)
    c: Coincident(g241,g232)
    c: Coincident(g241,g56)
    c: Coincident(g242,g56)
    c: Coincident(g242,g238)
    c: Coincident(g243,g238)
    c: Coincident(g243,g232)
    c: Vertical(g243)
    c: Horizontal(g244)
    c: Horizontal(g245)
    c: Horizontal(g246)
    c: Vertical(g249)
    c: Horizontal(g250)
    c: Vertical(g251)
    c: Distance(g246) = 4
    c: Distance(g250) = 4
    c: Distance(g249) = 4
    c: Distance(g251) = 4
    c: Distance(g244) = 4
    c: Distance(g245) = 4
FEATURE [Sketcher::SketchObject] Sketch001
  FullyConstrained = true
  MapMode = 4
  Placement = pos=(0,0,0) rot=(0.57735,0.57735,0.57735;2.0944rad)
  Support = -> [Sketch]
  sketch-geometry (46):
    g0: BSplineCurve PolesCount=3 KnotsCount=2 Degree=2 IsPeriodic=0
    g1: ArcOfCircle CenterX=73.1223 CenterY=-32.291 CenterZ=0 NormalX=0 NormalY=0 NormalZ=1 AngleXU=0 Radius=13 StartAngle=5.92268 EndAngle=9.06428
    g2: ArcOfCircle CenterX=66.7816 CenterY=-49.1439 CenterZ=0 NormalX=0 NormalY=0 NormalZ=1 AngleXU=0 Radius=13 StartAngle=2.78068 EndAngle=5.92131
    g3: ArcOfCircle CenterX=55.9263 CenterY=-78.1807 CenterZ=0 NormalX=0 NormalY=0 NormalZ=1 AngleXU=0 Radius=13 StartAngle=5.92268 EndAngle=9.06428
    g4: ArcOfCircle CenterX=49.5884 CenterY=-95.0342 CenterZ=0 NormalX=0 NormalY=0 NormalZ=1 AngleXU=0 Radius=13 StartAngle=2.78068 EndAngle=5.92131
    g5: ArcOfCircle CenterX=38.7206 CenterY=-124.067 CenterZ=0 NormalX=0 NormalY=0 NormalZ=1 AngleXU=0 Radius=13 StartAngle=5.92268 EndAngle=9.06428
    g6: ArcOfCircle CenterX=32.3875 CenterY=-140.92 CenterZ=0 NormalX=0 NormalY=0 NormalZ=1 AngleXU=0 Radius=13 StartAngle=2.78068 EndAngle=5.92131
    g7: ArcOfCircle CenterX=21.4715 CenterY=-169.934 CenterZ=0 NormalX=0 NormalY=0 NormalZ=1 AngleXU=0 Radius=13 StartAngle=5.92268 EndAngle=9.06428
    g8: ArcOfCircle CenterX=15.1336 CenterY=-186.787 CenterZ=0 NormalX=0 NormalY=0 NormalZ=1 AngleXU=0 Radius=13 StartAngle=2.78068 EndAngle=5.92131
    g9-g12: Circle x4 (B-spline internal-alignment scaffolding for g13; pole/knot coordinates omitted)
    g13: BSplineCurve PolesCount=4 KnotsCount=2 Degree=3 IsPeriodic=0
    g14: GeomPoint X=28.8094 Y=-19.0875 Z=0
    g15: GeomPoint X=47.0443 Y=-50.4712 Z=0
    g16: Circle CenterX=53.5586 CenterY=-23.2695 CenterZ=0 NormalX=0 NormalY=0 NormalZ=1 AngleXU=0 Radius=3.24518
    g17: Circle CenterX=-195.441 CenterY=-127.082 CenterZ=0 NormalX=0 NormalY=0 NormalZ=1 AngleXU=0 Radius=1
    g18: Circle CenterX=-8.24091 CenterY=-197.481 CenterZ=0 NormalX=0 NormalY=0 NormalZ=1 AngleXU=0 Radius=1
    g19: Circle CenterX=12.8789 CenterY=-141.321 CenterZ=0 NormalX=0 NormalY=0 NormalZ=1 AngleXU=0 Radius=1
    g20: BSplineCurve PolesCount=3 KnotsCount=2 Degree=2 IsPeriodic=0
    g21: GeomPoint X=-195.441 Y=-127.082 Z=0
    g22: GeomPoint X=12.8789 Y=-141.321 Z=0
    g23: Circle CenterX=-12.8016 CenterY=-179.036 CenterZ=0 NormalX=0 NormalY=0 NormalZ=1 AngleXU=0 Radius=10.5072
    g24: Circle CenterX=0.933922 CenterY=-166.43 CenterZ=0 NormalX=0 NormalY=0 NormalZ=1 AngleXU=0 Radius=3.26661
    g25: Circle CenterX=-33.5518 CenterY=-176.44 CenterZ=0 NormalX=0 NormalY=0 NormalZ=1 AngleXU=0 Radius=5.64388
    g26: Circle CenterX=-47.2366 CenterY=-173.859 CenterZ=0 NormalX=0 NormalY=0 NormalZ=1 AngleXU=0 Radius=3.01653
    g27: Circle CenterX=-56.2595 CenterY=-171.456 CenterZ=0 NormalX=0 NormalY=0 NormalZ=1 AngleXU=0 Radius=2.12826
    g28: ArcOfCircle CenterX=51.2151 CenterY=-198.473 CenterZ=0 NormalX=0 NormalY=0 NormalZ=1 AngleXU=0 Radius=20 StartAngle=2.78189 EndAngle=4.35269
    g29: LineSegment StartX=32.4951 StartY=-191.433 StartZ=0 EndX=94.6578 EndY=-26.1352 EndZ=0
    g30: LineSegment StartX=43.1192 StartY=-220.001 StartZ=0 EndX=-196.497 EndY=-129.89 EndZ=0
    g31: LineSegment StartX=43.1192 StartY=-220.001 StartZ=0 EndX=44.1752 EndY=-217.193 EndZ=0
    g32: LineSegment StartX=117.223 StartY=-19.0875 StartZ=0 EndX=117.223 EndY=-16.0875 EndZ=0
    g33: LineSegment StartX=117.223 StartY=-16.0875 StartZ=0 EndX=17.2232 EndY=-16.0875 EndZ=0
    g34: LineSegment StartX=17.2232 StartY=-16.0875 StartZ=0 EndX=17.2232 EndY=-19.0875 EndZ=0
    g35: LineSegment StartX=28.8094 StartY=-19.0875 StartZ=0 EndX=17.2232 EndY=-19.0875 EndZ=0
    g36: LineSegment StartX=47.0443 StartY=-50.4712 StartZ=0 EndX=12.8789 EndY=-141.321 EndZ=0
    g37: LineSegment StartX=-195.441 StartY=-127.082 StartZ=0 EndX=-196.497 EndY=-129.89 EndZ=0
    g38: LineSegment StartX=85.2866 StartY=-36.8766 StartZ=0 EndX=78.9396 EndY=-53.7463 EndZ=0
    g39: LineSegment StartX=60.9579 StartY=-27.7053 StartZ=0 EndX=54.6191 EndY=-44.5532 EndZ=0
    g40: LineSegment StartX=68.0907 StartY=-82.7664 StartZ=0 EndX=61.7465 EndY=-99.6365 EndZ=0
    g41: LineSegment StartX=43.7619 StartY=-73.595 StartZ=0 EndX=37.426 EndY=-90.4435 EndZ=0
    g42: LineSegment StartX=50.885 StartY=-128.652 StartZ=0 EndX=44.5456 EndY=-145.522 EndZ=0
    g43: LineSegment StartX=26.5562 StartY=-119.481 StartZ=0 EndX=20.2251 EndY=-136.329 EndZ=0
    g44: LineSegment StartX=9.3071 StartY=-165.349 StartZ=0 EndX=2.97115 EndY=-182.197 EndZ=0
    g45: LineSegment StartX=33.6358 StartY=-174.52 StartZ=0 EndX=27.2917 EndY=-191.39 EndZ=0
  constraints (71):
    c: Block(g0)
    c: Block(g1)
    c: Block(g2)
    c: Block(g4)
    c: Block(g3)
    c: Block(g6)
    c: Block(g5)
    c: Block(g8)
    c: Block(g7)
    c: Weight(g9) = 1
    c: Equal(g9,g10)
    c: Equal(g9,g11)
    c: Equal(g9,g12)
    c: InternalAlignment(g9-g12 -> g13) x4
    c: InternalAlignment(g14,g13)
    c: InternalAlignment(g15,g13)
    c: Block(g16)
    c: Weight(g17) = 1
    c: Equal(g17,g18)
    c: Equal(g17,g19)
    c: InternalAlignment(g17,g20)
    c: InternalAlignment(g18,g20)
    c: InternalAlignment(g19,g20)
    c: InternalAlignment(g21,g20)
    c: InternalAlignment(g22,g20)
    c: Block(g20)
    c: Block(g23)
    c: Block(g24)
    c: Block(g25)
    c: Block(g26)
    c: Block(g27)
    c: Block(g28)
    c: Coincident(g29,g28)
    c: Coincident(g29,g0)
    c: Block(g13)
    c: Coincident(g31,g30)
    c: Coincident(g31,g28)
    c: Block(g31)
    c: Coincident(g32,g0)
    c: Vertical(g32)
    c: Coincident(g33,g32)
    c: Horizontal(g33)
    c: Coincident(g34,g33)
    c: Vertical(g34)
    c: Block(g33)
    c: Coincident(g35,g13)
    c: Coincident(g35,g34)
    c: Horizontal(g35)
    c: Coincident(g36,g13)
    c: Coincident(g36,g20)
    c: Coincident(g37,g20)
    c: Coincident(g37,g30)
    c: Block(g30)
    c: Coincident(g38,g1)
    c: Coincident(g38,g2)
    c: Coincident(g39,g1)
    c: Coincident(g39,g2)
    c: Coincident(g40,g3)
    c: Coincident(g40,g4)
    c: Coincident(g41,g3)
    c: Coincident(g41,g4)
    c: Coincident(g42,g5)
    c: Coincident(g42,g6)
    c: Coincident(g43,g5)
    c: Coincident(g43,g6)
    c: Coincident(g44,g7)
    c: Coincident(g44,g8)
    c: Coincident(g45,g7)
    c: Coincident(g45,g8)
    c: Distance(g30) = 256
    c: Distance(g33) = 100
FEATURE [Part::Extrusion] Extrude002
  Base = -> Sketch001
  Dir = (1,0,0)
  DirMode = 2
  FaceMakerClass = Part::FaceMakerBullseye
  LengthFwd = 8
  LengthRev = 0
  Solid = true
  Symmetric = false
FEATURE [Sketcher::SketchObject] Sketch002
  FullyConstrained = true
  sketch-geometry (20):
    g0: LineSegment StartX=-2.77179 StartY=-200.304 StartZ=0 EndX=5.22821 EndY=-200.304 EndZ=0
    g1: LineSegment StartX=5.22821 StartY=-200.304 StartZ=0 EndX=5.22821 EndY=-197.304 EndZ=0
    g2: LineSegment StartX=-2.77179 StartY=-200.304 StartZ=0 EndX=-2.77179 EndY=-197.304 EndZ=0
    g3: LineSegment StartX=5.22821 StartY=-197.304 StartZ=0 EndX=8.22821 EndY=-197.304 EndZ=0
    g4: LineSegment StartX=-2.77179 StartY=-197.304 StartZ=0 EndX=-5.77179 EndY=-197.304 EndZ=0
    g5: LineSegment StartX=19.2282 StartY=-203.304 StartZ=0 EndX=19.2282 EndY=-206.304 EndZ=0
    g6: LineSegment StartX=-16.7718 StartY=-203.304 StartZ=0 EndX=-16.7718 EndY=-206.304 EndZ=0
    g7: LineSegment StartX=-16.7718 StartY=-206.304 StartZ=0 EndX=19.2282 EndY=-206.304 EndZ=0
    g8: Circle CenterX=-16.7718 CenterY=-203.304 CenterZ=0 NormalX=0 NormalY=0 NormalZ=1 AngleXU=0 Radius=1
    g9: Circle CenterX=-5.77179 CenterY=-203.304 CenterZ=0 NormalX=0 NormalY=0 NormalZ=1 AngleXU=0 Radius=1
    g10: Circle CenterX=-5.77179 CenterY=-197.304 CenterZ=0 NormalX=0 NormalY=0 NormalZ=1 AngleXU=0 Radius=1
    g11: BSplineCurve PolesCount=3 KnotsCount=2 Degree=2 IsPeriodic=0
    g12: GeomPoint X=-16.7718 Y=-203.304 Z=0
    g13: GeomPoint X=-5.77179 Y=-197.304 Z=0
    g14: Circle CenterX=19.2282 CenterY=-203.304 CenterZ=0 NormalX=0 NormalY=0 NormalZ=1 AngleXU=0 Radius=1
    g15: Circle CenterX=8.22821 CenterY=-203.304 CenterZ=0 NormalX=0 NormalY=0 NormalZ=1 AngleXU=0 Radius=1
    g16: Circle CenterX=8.22821 CenterY=-197.304 CenterZ=0 NormalX=0 NormalY=0 NormalZ=1 AngleXU=0 Radius=1
    g17: BSplineCurve PolesCount=3 KnotsCount=2 Degree=2 IsPeriodic=0
    g18: GeomPoint X=19.2282 Y=-203.304 Z=0
    g19: GeomPoint X=8.22821 Y=-197.304 Z=0
  constraints (41):
    c: Horizontal(g0)
    c: Distance(g0) = 8
    c: Coincident(g1,g0)
    c: Vertical(g1)
    c: Distance(g1) = 3
    c: Coincident(g2,g0)
    c: Vertical(g2)
    c: Distance(g2) = 3
    c: Coincident(g3,g1)
    c: Horizontal(g3)
    c: Distance(g3) = 3
    c: Coincident(g4,g2)
    c: Horizontal(g4)
    c: Distance(g4) = 3
    c: Vertical(g5)
    c: Vertical(g6)
    c: Coincident(g7,g6)
    c: Coincident(g7,g5)
    c: Weight(g8) = 1
    c: Equal(g8,g9)
    c: Equal(g8,g10)
    c: Coincident(g11,g4)
    c: InternalAlignment(g8,g11)
    c: InternalAlignment(g9,g11)
    c: InternalAlignment(g10,g11)
    c: InternalAlignment(g12,g11)
    c: InternalAlignment(g13,g11)
    c: Coincident(g17,g5)
    c: Weight(g14) = 1
    c: Equal(g14,g15)
    c: Equal(g14,g16)
    c: Coincident(g17,g3)
    c: InternalAlignment(g14,g17)
    c: InternalAlignment(g15,g17)
    c: InternalAlignment(g16,g17)
    c: InternalAlignment(g18,g17)
    c: InternalAlignment(g19,g17)
    c: Block(g7)
    c: Block(g17)
    c: Block(g11)
    c: Block(g6)
FEATURE [Part::Extrusion] Extrude003
  Base = -> Sketch002
  Dir = (0,0,1)
  DirMode = 2
  FaceMakerClass = Part::FaceMakerBullseye
  LengthFwd = 260
  LengthRev = 0
  Solid = true
  Symmetric = false
FEATURE [Part::Extrusion] Extrude
  Base = -> Sketch
  Dir = (0,0,1)
  DirMode = 2
  FaceMakerClass = Part::FaceMakerBullseye
  LengthFwd = 14
  LengthRev = 0
  Solid = true
  Symmetric = false
